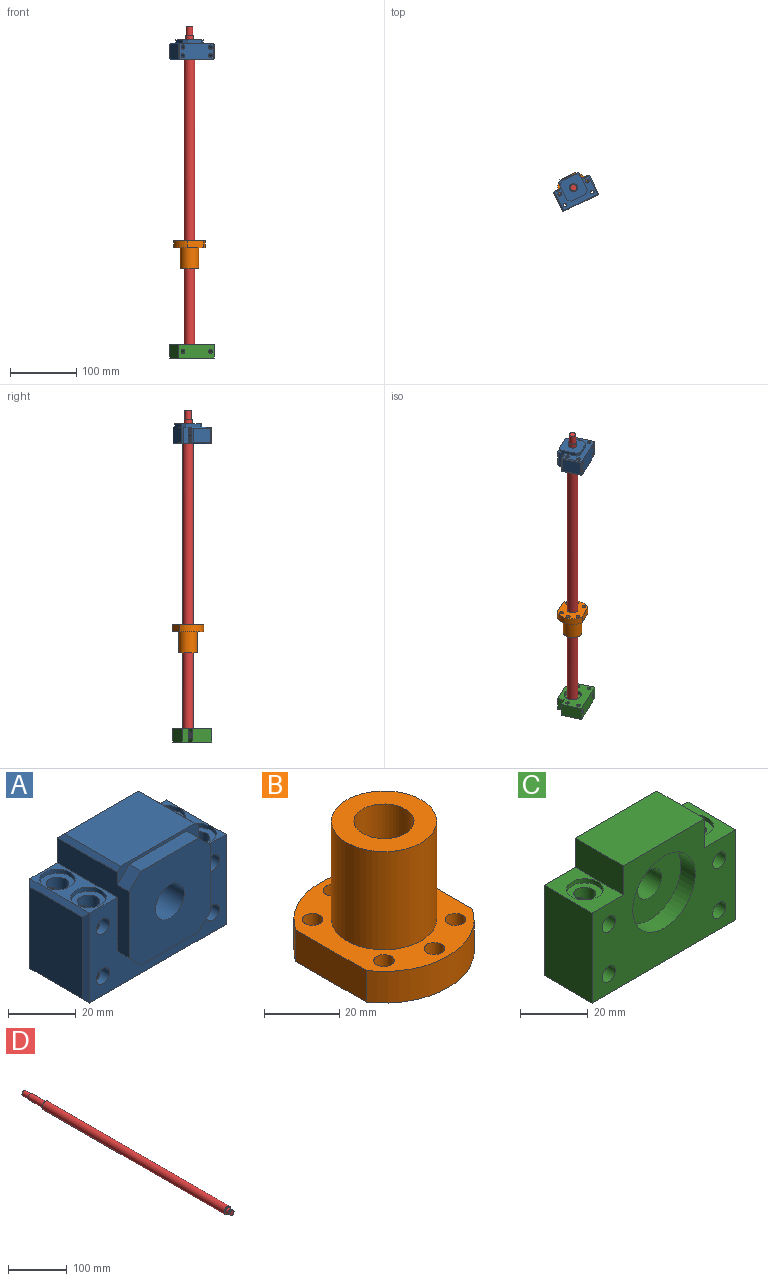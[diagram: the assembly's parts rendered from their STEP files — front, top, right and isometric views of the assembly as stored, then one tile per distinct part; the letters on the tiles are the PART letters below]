
ASSEMBLY  parts=4 mates=5
PART A: 54 faces, bbox 60x30x43 mm
  f0: cylinder r=3.3mm len=31mm, axis (0,0,1), area 535.9mm2, adj f5,f7,f10,f43,f44,f53
  f1: cylinder r=3.3mm len=31mm, axis (0,0,1), area 535.9mm2, adj f4,f6,f10,f43,f44,f51
  f2: cylinder r=3.3mm len=31mm, axis (0,0,1), area 535.9mm2, adj f10,f19,f20,f41,f42,f48
  f3: cylinder r=3.3mm len=31mm, axis (0,0,1), area 535.9mm2, adj f8,f9,f10,f41,f42,f46
  f4: cylinder r=2.75mm len=5.5mm, axis (0,1,0), area 58.5mm2, adj f1,f22
  f5: cylinder r=2.75mm len=5.5mm, axis (0,1,0), area 58.5mm2, adj f0,f11
  f6: cylinder r=2.75mm len=5.5mm, axis (0,1,0), area 58.5mm2, adj f1,f22
  f7: cylinder r=2.75mm len=5.5mm, axis (0,1,0), area 58.5mm2, adj f0,f11
  f8: cylinder r=2.75mm len=5.5mm, axis (0,1,0), area 58.5mm2, adj f3,f11
  f9: cylinder r=2.75mm len=5.5mm, axis (0,1,0), area 58.5mm2, adj f3,f11
  f10: plane 57x25mm, normal (0,0,-1), area 1288.2mm2, adj f0,f1,f2,f3,f11,f22,f33,f37
  f11: plane 57x32.5mm, normal (0,-1,0), area 949.5mm2, adj f5,f7,f8,f9,f10,f13,f14,f16
  f12: plane 29.5x22mm, normal (1,0,0), area 649mm2, adj f30,f31,f32,f33
  f13: plane 25x11.5mm, normal (0,0,1), area 114.3mm2, adj f11,f14,f22,f30,f47,f49
  f14: plane 30x28.5mm, normal (1,0,0), area 345mm2, adj f11,f13,f21,f22,f25,f27,f28,f38
  f15: plane 31x23.5mm, normal (0,0,1), area 728.5mm2, adj f21,f38,f39,f40
  f16: plane 30x28.5mm, normal (-1,0,0), area 345mm2, adj f11,f17,f21,f22,f25,f26,f29,f39
  f17: plane 25x11.5mm, normal (0,0,1), area 114.3mm2, adj f11,f16,f22,f34,f50,f52
  f18: plane 29.5x22mm, normal (-1,0,0), area 649mm2, adj f34,f35,f36,f37
  f19: cylinder r=2.75mm len=5.5mm, axis (0,1,0), area 58.5mm2, adj f2,f22
  f20: cylinder r=2.75mm len=5.5mm, axis (0,1,0), area 58.5mm2, adj f2,f22
  f21: plane 34x6mm, normal (0,-1,0), area 56.8mm2, adj f14,f15,f16,f23,f28,f29,f38,f39
  f22: plane 57x41.5mm, normal (0,1,0), area 1950.4mm2, adj f4,f6,f10,f13,f14,f16,f17,f19
  f23: plane 24x5mm, normal (0,0,1), area 120mm2, adj f21,f25,f28,f29
  f24: plane 24x5mm, normal (0,0,-1), area 120mm2, adj f11,f25,f26,f27
  f25: plane 34x34mm, normal (0,-1,0), area 992.9mm2, adj f14,f16,f23,f24,f26,f27,f28,f29
  f26: plane 5x5mm, normal (-0.71,0,-0.71), area 35.4mm2, adj f11,f16,f24,f25
  f27: plane 5x5mm, normal (0.71,0,-0.71), area 35.4mm2, adj f11,f14,f24,f25
  f28: plane 5x5mm, normal (0.71,0,0.71), area 35.4mm2, adj f14,f21,f23,f25
  f29: plane 5x5mm, normal (-0.71,0,0.71), area 35.4mm2, adj f16,f21,f23,f25
  f30: plane 25x1.5mm, normal (0.71,0,0.71), area 49.9mm2, adj f12,f13,f31,f32
  f31: plane 32.5x1.5mm, normal (0.71,-0.71,0), area 65.8mm2, adj f11,f12,f30,f33
  f32: plane 32.5x1.5mm, normal (0.71,0.71,0), area 65.8mm2, adj f12,f22,f30,f33
  f33: plane 25x1.5mm, normal (0.71,0,-0.71), area 49.9mm2, adj f10,f12,f31,f32
  f34: plane 25x1.5mm, normal (-0.71,0,0.71), area 49.9mm2, adj f17,f18,f35,f36
  f35: plane 32.5x1.5mm, normal (-0.71,-0.71,0), area 65.8mm2, adj f11,f18,f34,f37
  f36: plane 32.5x1.5mm, normal (-0.71,0.71,0), area 65.8mm2, adj f18,f22,f34,f37
  f37: plane 25x1.5mm, normal (-0.71,0,-0.71), area 49.9mm2, adj f10,f18,f35,f36
  f38: plane 25x1.5mm, normal (0.71,0,0.71), area 51.4mm2, adj f14,f15,f21,f40
  f39: plane 25x1.5mm, normal (-0.71,0,0.71), area 51.4mm2, adj f15,f16,f21,f40
  f40: plane 34x1.5mm, normal (0,0.71,0.71), area 68.9mm2, adj f15,f22,f38,f39
  f41: cylinder r=2.75mm len=9.35mm, axis (0,1,0), area 134.2mm2, adj f2,f3
  f42: cylinder r=2.75mm len=9.35mm, axis (0,1,0), area 134.2mm2, adj f2,f3
  f43: cylinder r=2.75mm len=9.35mm, axis (0,1,0), area 134.2mm2, adj f0,f1
  f44: cylinder r=2.75mm len=9.35mm, axis (0,1,0), area 134.2mm2, adj f0,f1
  f45: cylinder r=6mm len=30mm, axis (0,-1,0), area 1131mm2, adj f22,f25
  f46: plane 10.5x10.5mm, normal (0,0,1), area 52.4mm2, adj f3,f47
  f47: cylinder r=5.25mm len=10.5mm, axis (0,0,1), area 49.5mm2, adj f13,f46
  f48: plane 10.5x10.5mm, normal (0,0,1), area 52.4mm2, adj f2,f49
  f49: cylinder r=5.25mm len=10.5mm, axis (0,0,1), area 49.5mm2, adj f13,f48
  f50: cylinder r=5.25mm len=10.5mm, axis (0,0,1), area 49.5mm2, adj f17,f51
  f51: plane 10.5x10.5mm, normal (0,0,1), area 52.4mm2, adj f1,f50
  f52: cylinder r=5.25mm len=10.5mm, axis (0,0,1), area 49.5mm2, adj f17,f53
  f53: plane 10.5x10.5mm, normal (0,0,1), area 52.4mm2, adj f0,f52
PART B: 15 faces, bbox 40x48x42.3 mm
  f0: plane 26.53x10.3mm, normal (-1,0,0), area 273.3mm2, adj f1,f3,f11,f12
  f1: cylinder r=24mm len=40mm, axis (0,0,-1), area 487mm2, adj f0,f2,f11,f12
  f2: plane 26.53x10.3mm, normal (1,0,0), area 273.3mm2, adj f1,f3,f11,f12
  f3: cylinder r=24mm len=40mm, axis (0,0,-1), area 487mm2, adj f0,f2,f11,f12
  f4: cylinder r=2.75mm len=10.3mm, axis (0,0,-1), area 178mm2, adj f11,f12
  f5: cylinder r=2.75mm len=10.3mm, axis (0,0,-1), area 178mm2, adj f11,f12
  f6: cylinder r=2.75mm len=10.3mm, axis (0,0,-1), area 178mm2, adj f11,f12
  f7: cylinder r=2.75mm len=10.3mm, axis (0,0,-1), area 178mm2, adj f11,f12
  f8: cylinder r=2.75mm len=10.3mm, axis (0,0,-1), area 178mm2, adj f11,f12
  f9: cylinder r=2.75mm len=10.3mm, axis (0,0,-1), area 178mm2, adj f11,f12
  f10: cylinder r=8mm len=42.3mm, axis (0,0,-1), area 2126.2mm2, adj f12,f14
  f11: plane 48x40mm, normal (0,0,1), area 907.2mm2, adj f0,f1,f2,f3,f4,f5,f6,f7
  f12: plane 48x40mm, normal (0,0,-1), area 1321.9mm2, adj f0,f1,f2,f3,f4,f5,f6,f7
  f13: cylinder r=14mm len=32mm, axis (0,0,-1), area 2814.9mm2, adj f11,f14
  f14: plane 28x28mm, normal (0,0,1), area 414.7mm2, adj f10,f13
PART C: 29 faces, bbox 60x20x43 mm
  f0: cylinder r=3.25mm len=31mm, axis (0,0,1), area 525.7mm2, adj f2,f3,f8,f18,f19,f27
  f1: cylinder r=3.25mm len=31mm, axis (0,0,1), area 525.7mm2, adj f4,f5,f6,f7,f8,f26
  f2: cylinder r=2.75mm len=8.27mm, axis (0,1,0), area 128.7mm2, adj f0,f20
  f3: cylinder r=2.75mm len=8.27mm, axis (0,1,0), area 128.7mm2, adj f0,f20
  f4: cylinder r=2.75mm len=8.27mm, axis (0,1,0), area 128.7mm2, adj f1,f20
  f5: cylinder r=2.75mm len=8.27mm, axis (0,1,0), area 128.7mm2, adj f1,f21
  f6: cylinder r=2.75mm len=8.27mm, axis (0,1,0), area 128.7mm2, adj f1,f20
  f7: cylinder r=2.75mm len=8.27mm, axis (0,1,0), area 128.7mm2, adj f1,f21
  f8: plane 60x20mm, normal (0,0,-1), area 1133.6mm2, adj f0,f1,f10,f16,f20,f21
  f9: cylinder r=13mm len=26mm, axis (0,1,0), area 490.1mm2, adj f21,f24
  f10: plane 32.5x20mm, normal (1,0,0), area 650mm2, adj f8,f11,f20,f21
  f11: plane 20x13mm, normal (0,0,1), area 168.4mm2, adj f10,f12,f20,f21,f25
  f12: plane 20x10.5mm, normal (1,0,0), area 210mm2, adj f11,f13,f20,f21
  f13: plane 34x20mm, normal (0,0,1), area 680mm2, adj f12,f14,f20,f21
  f14: plane 20x10.5mm, normal (-1,0,0), area 210mm2, adj f13,f15,f20,f21
  f15: plane 20x13mm, normal (0,0,1), area 168.4mm2, adj f14,f16,f20,f21,f28
  f16: plane 32.5x20mm, normal (-1,0,0), area 650mm2, adj f8,f15,f20,f21
  f17: cylinder r=13mm len=26mm, axis (0,1,0), area 490.1mm2, adj f20,f23
  f18: cylinder r=2.75mm len=8.27mm, axis (0,1,0), area 128.7mm2, adj f0,f21
  f19: cylinder r=2.75mm len=8.27mm, axis (0,1,0), area 128.7mm2, adj f0,f21
  f20: plane 60x43mm, normal (0,-1,0), area 1681mm2, adj f2,f3,f4,f6,f8,f10,f11,f12
  f21: plane 60x43mm, normal (0,1,0), area 1681mm2, adj f5,f7,f8,f9,f10,f11,f12,f13
  f22: cylinder r=5mm len=10mm, axis (0,1,0), area 251.3mm2, adj f23,f24
  f23: plane 26x26mm, normal (0,-1,0), area 452.4mm2, adj f17,f22
  f24: plane 26x26mm, normal (0,1,0), area 452.4mm2, adj f9,f22
  f25: cylinder r=5.4mm len=10.8mm, axis (0,0,1), area 50.9mm2, adj f11,f26
  f26: plane 10.8x10.8mm, normal (0,0,1), area 58.4mm2, adj f1,f25
  f27: plane 10.8x10.8mm, normal (0,0,1), area 58.4mm2, adj f0,f28
  f28: cylinder r=5.4mm len=10.8mm, axis (0,0,1), area 50.9mm2, adj f15,f27
PART D: 13 faces, bbox 16x500x16 mm
  f0: cylinder r=5mm len=10mm, axis (0,-1,0), area 215.2mm2, adj f3,f9
  f1: cylinder r=6mm len=36mm, axis (0,1,0), area 1357.2mm2, adj f4,f6
  f2: cylinder r=8mm len=438mm, axis (0,1,0), area 22016.3mm2, adj f3,f4
  f3: plane 16x16mm, normal (0,-1,0), area 122.5mm2, adj f0,f2
  f4: plane 16x16mm, normal (0,1,0), area 88mm2, adj f1,f2
  f5: cylinder r=5mm len=15mm, axis (0,1,0), area 471.2mm2, adj f6,f7
  f6: plane 12x12mm, normal (0,1,0), area 34.6mm2, adj f1,f5
  f7: plane 10x10mm, normal (0,1,0), area 78.5mm2, adj f5
  f8: cylinder r=4.5mm len=9mm, axis (0,-1,0), area 32.5mm2, adj f9,f10
  f9: plane 10x10mm, normal (0,-1,0), area 14.9mm2, adj f0,f8
  f10: plane 10x10mm, normal (0,1,0), area 14.9mm2, adj f8,f12
  f11: plane 10x10mm, normal (0,-1,0), area 78.5mm2, adj f12
  f12: cylinder r=5mm len=10mm, axis (0,-1,0), area 94.2mm2, adj f10,f11
PLACE A rot(axis=(-0.95,-0.21,0.21),92.8deg) t=(-1.99,-7.69,153.34)mm
PLACE B rot(axis=(-0.84,0.53,0),180deg) t=(-1.99,-7.69,-120.96)mm
PLACE C rot(axis=(-0.95,-0.21,0.21),92.8deg) t=(1.75,-15.6,-288.66)mm
PLACE D rot(axis=(1,0,0),90deg) t=(-1.99,-7.69,-45.66)mm fixed
MATE cylindrical D.f2 <-> B.f10  axis (0,0,1) through (-1.99,-7.69,-65.66)mm
MATE revolute D.f1 <-> A.f45  axis (0,0,1) through (-1.99,-7.69,153.34)mm
MATE parallel C.f13 <-> B.f0  axis (-0.43,0.9,0) through (-9.69,8.58,-298.66)mm
MATE parallel B.f0 <-> A.f15  axis (-0.43,0.9,0) through (-10.55,10.39,-126.11)mm
MATE revolute C.f22 <-> D.f2  axis (0,0,1) through (-1.99,-7.69,-284.66)mm
